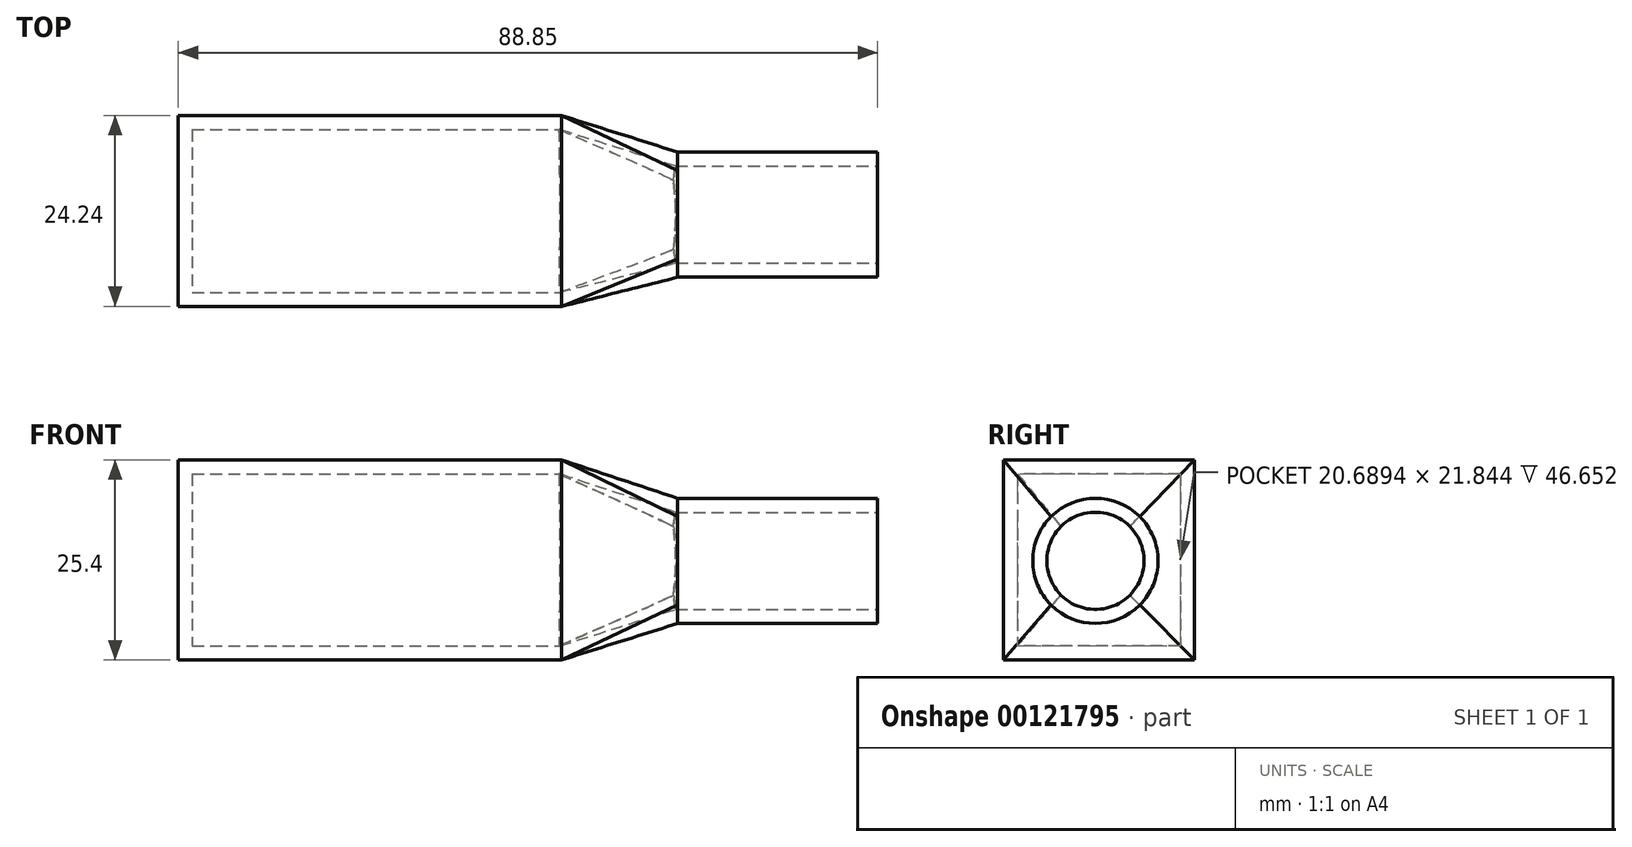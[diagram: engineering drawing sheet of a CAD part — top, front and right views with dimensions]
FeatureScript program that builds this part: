
annotation { "Feature Type Name" : "Feature", "Feature Type Description" : "" }
export const myFeature = defineFeature(function(context is Context, id is Id, definition is map)
    precondition{}
    {
        {
            var Q0;
            Q0=qCreatedBy(makeId("Top.planeOp"),FACE);
            var sketch = newSketch(context, id + "F0", { "sketchPlane" : qUnion([Q0])});
            skLineSegment(sketch, "E0.bottom", {"start": v(-38.33, 45.37) * mm, "end": v(10.4, 45.37) * mm});
            skLineSegment(sketch, "E0.top", {"start": v(-38.33, 21.13) * mm, "end": v(10.4, 21.13) * mm});
            skLineSegment(sketch, "E0.left", {"start": v(-38.33, 45.37) * mm, "end": v(-38.33, 21.13) * mm});
            skLineSegment(sketch, "E0.right", {"start": v(10.4, 45.37) * mm, "end": v(10.4, 21.13) * mm});
            skSolve(sketch);
        }
        {
            var Q0;
            Q0=makeQuery(id+"F0.imprint","IMPRINT",FACE,{"disambiguationData":[TD([[makeQuery(id+"F0.imprint","IMPRINT",EDGE,{"derivedFrom":sQuery(id+"F0.wireOp",EDGE,"E0.bottom")}),-1.0]])]});
            extrude(context, id + "F1", {"entities" : qUnion([Q0]), "depth" : 25.4 * mm});
        }
        {
            var Q0;
            Q0=makeQuery(id+"F1.opExtrude","SWEPT_FACE",FACE,{"disambiguationData":[OSD([sQuery(id+"F0.wireOp",EDGE,"E0.right")])]});
            cPlane(context, id + "F2", {"entities" : qUnion([Q0]), "cplaneType" : CPlaneType.OFFSET, "offset" : 14.73 * mm, "width" : 152.4 * mm, "height" : 152.4 * mm});
        }
        {
            var Q0;
            Q0=qCreatedBy(id+"F2.planeOp",FACE);
            var sketch = newSketch(context, id + "F3", { "sketchPlane" : qUnion([Q0])});
            skCircle(sketch, "E1", {"center": v(32.79, 12.58) * mm, "radius": 7.95 * mm});
            skSolve(sketch);
        }
        {
            var Q1;
            Q1=makeQuery(id+"F1.opExtrude","SWEPT_FACE",FACE,{"disambiguationData":[OSD([sQuery(id+"F0.wireOp",EDGE,"E0.right")])]});
            var Q2;
            Q2=makeQuery(id+"F3.imprint","IMPRINT",FACE,{"disambiguationData":[TD([[makeQuery(id+"F3.imprint","IMPRINT",EDGE,{"derivedFrom":sQuery(id+"F3.wireOp",EDGE,"E1")}),1.0]])]});
            loft(context, id + "F4", {"operationType" : NewBodyOperationType.ADD, "sheetProfilesArray" : [{ "sheetProfileEntities" : qUnion([Q1]) }, { "sheetProfileEntities" : qUnion([Q2]) }]});
        }
        {
            var Q0;
            Q0=makeQuery(id+"F4.opLoft","CAP_FACE",FACE,{"disambiguationData":[OSD([makeQuery(id+"F3.imprint","IMPRINT",FACE,{"disambiguationData":[TD([[makeQuery(id+"F3.imprint","IMPRINT",EDGE,{"derivedFrom":sQuery(id+"F3.wireOp",EDGE,"E1")}),1.0]])]})])],"isStart":true});
            extrude(context, id + "F5", {"entities" : qUnion([Q0]), "operationType" : NewBodyOperationType.ADD, "depth" : 25.4 * mm});
        }
        {
            var Q0;
            Q0=makeQuery(id+"F5.opExtrude","CAP_FACE",FACE,{"disambiguationData":[OSD([makeQuery(id+"F3.imprint","IMPRINT",FACE,{"disambiguationData":[TD([[makeQuery(id+"F3.imprint","IMPRINT",EDGE,{"derivedFrom":sQuery(id+"F3.wireOp",EDGE,"E1")}),1.0]])]})])],"isStart":false});
            shell(context, id + "F6", {"entities" : qUnion([Q0]), "thickness" : 1.78 * mm});
        }
    });
